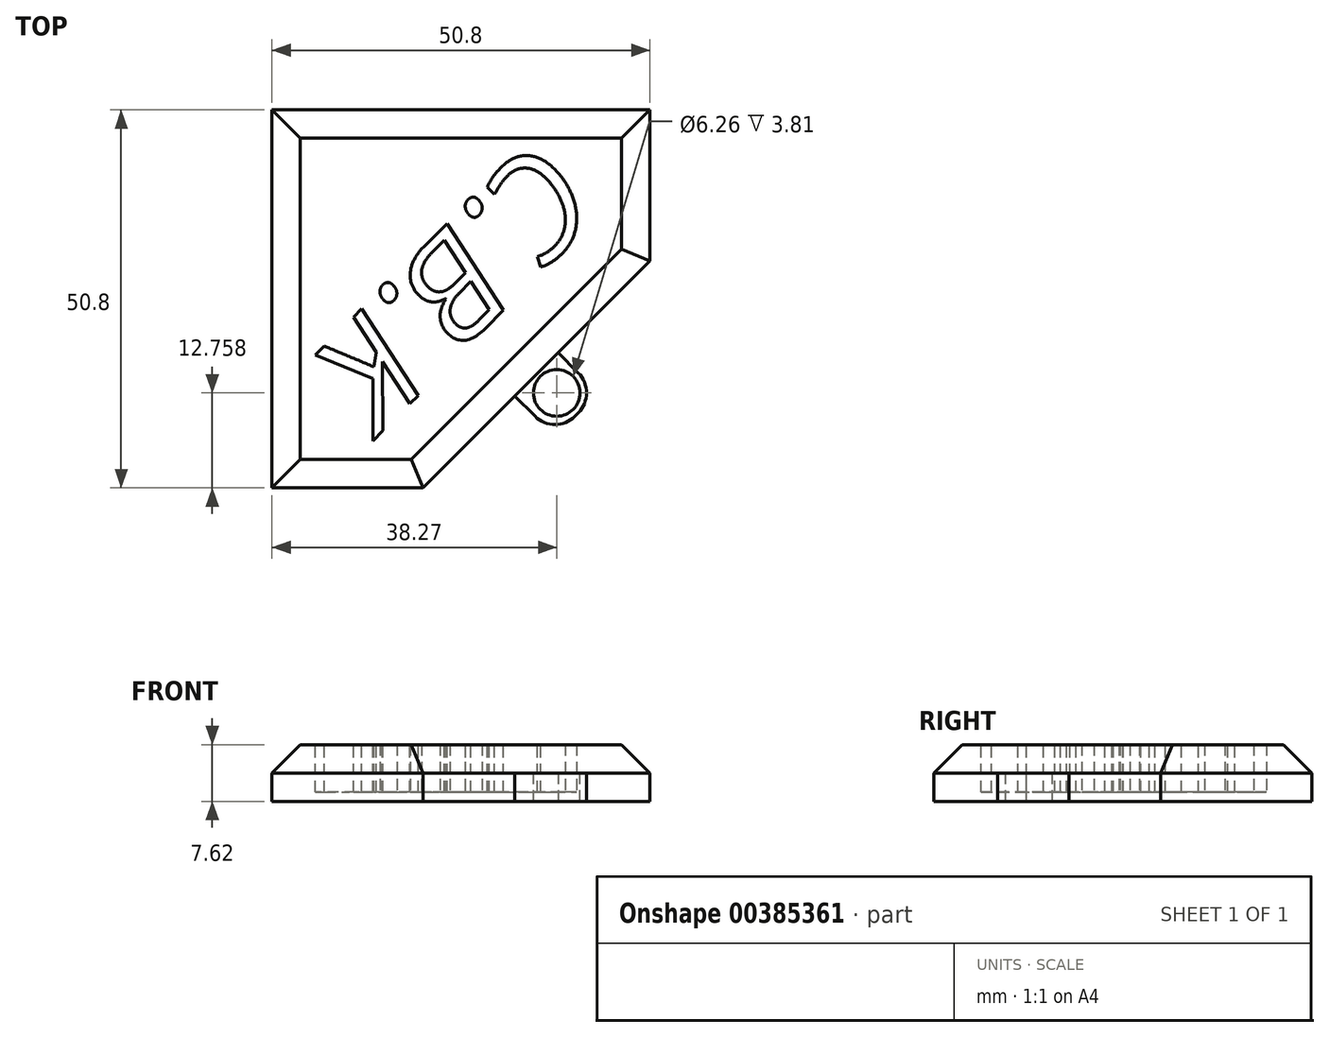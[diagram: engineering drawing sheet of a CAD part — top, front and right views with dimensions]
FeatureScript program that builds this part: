
annotation { "Feature Type Name" : "Feature", "Feature Type Description" : "" }
export const myFeature = defineFeature(function(context is Context, id is Id, definition is map)
    precondition{}
    {
        {
            var Q0;
            Q0=qCreatedBy(makeId("Top.planeOp"),FACE);
            var sketch = newSketch(context, id + "F0", { "sketchPlane" : qUnion([Q0])});
            skLineSegment(sketch, "E0.bottom", {"start": v(0, 0) * mm, "end": v(50.8, 0) * mm});
            skLineSegment(sketch, "E0.top", {"start": v(0, 50.8) * mm, "end": v(50.8, 50.8) * mm});
            skLineSegment(sketch, "E0.left", {"start": v(0, 0) * mm, "end": v(0, 50.8) * mm});
            skLineSegment(sketch, "E0.right", {"start": v(50.8, 0) * mm, "end": v(50.8, 50.8) * mm});
            skSolve(sketch);
        }
        {
            var Q0;
            Q0 = qSketchRegion(id + "F0", true);
            extrude(context, id + "F1", {"entities" : qUnion([Q0]), "oppositeDirection" : true, "depth" : 7.62 * mm});
        }
        {
            var Q0;
            Q0=makeQuery(id+"F1.opExtrude","SWEPT_EDGE",EDGE,{"disambiguationData":[OSD([sQuery(id+"F0.wireOp",EDGE,"E0.bottom"),sQuery(id+"F0.wireOp",EDGE,"E0.right")])]});
            chamfer(context, id + "F2", {"entities" : qUnion([Q0]), "width" : 30.48 * mm, "tangentPropagation" : true});
        }
        {
            var Q0;
            Q0=qCreatedBy(makeId("Top.planeOp"),FACE);
            var sketch = newSketch(context, id + "F3", { "sketchPlane" : qUnion([Q0])});
            skText(sketch, "E1", { "text": "C.B.K", "fontName": "OpenSans-Italic.ttf"});
            const initialGuessF3  = {"E1": [0.03539, 0.0474, -0.70703, -0.70719, 0.01372]};
            skSetInitialGuess(sketch, initialGuessF3);
            skSolve(sketch);
        }
        {
            var Q0;
            Q0 = qSketchRegion(id + "F3", true);
            extrude(context, id + "F4", {"entities" : qUnion([Q0]), "operationType" : NewBodyOperationType.REMOVE, "oppositeDirection" : true, "depth" : 6.35 * mm});
        }
        {
            var Q0;
            Q0=makeQuery(id+"F1.opExtrude","CAP_EDGE",EDGE,{"disambiguationData":[OSD([sQuery(id+"F0.wireOp",EDGE,"E0.right")])],"isStart":true});
            chamfer(context, id + "F5", {"entities" : qUnion([Q0]), "width" : 3.8 * mm, "tangentPropagation" : true});
        }
        {
            var Q0;
            {var subQ0=sQuery(id+"F0.wireOp",EDGE,"E0.right");var subQ1=sQuery(id+"F0.wireOp",EDGE,"E0.bottom");Q0=makeQuery(id+"F2.opChamfer","BLEND_EDGE",EDGE,{"blendedFrom":[makeQuery(id+"F1.opExtrude","SWEPT_EDGE",EDGE,{"disambiguationData":[OSD([subQ1,subQ0])]}),makeQuery(id+"F1.opExtrude","CAP_FACE",FACE,{"disambiguationData":[OSD([subQ1,sQuery(id+"F0.wireOp",EDGE,"E0.top"),sQuery(id+"F0.wireOp",EDGE,"E0.left"),subQ0])],"isStart":true})],"blendedInto":[makeQuery(id+"F1.opExtrude","CAP_FACE",FACE,{"disambiguationData":[OSD([subQ1,sQuery(id+"F0.wireOp",EDGE,"E0.top"),sQuery(id+"F0.wireOp",EDGE,"E0.left"),subQ0])],"isStart":true})]});}
            var Q1;
            Q1=makeQuery(id+"F1.opExtrude","CAP_EDGE",EDGE,{"disambiguationData":[OSD([sQuery(id+"F0.wireOp",EDGE,"E0.bottom")])],"isStart":true});
            var Q2;
            Q2=makeQuery(id+"F1.opExtrude","CAP_EDGE",EDGE,{"disambiguationData":[OSD([sQuery(id+"F0.wireOp",EDGE,"E0.top")])],"isStart":true});
            var Q3;
            Q3=makeQuery(id+"F1.opExtrude","CAP_EDGE",EDGE,{"disambiguationData":[OSD([sQuery(id+"F0.wireOp",EDGE,"E0.left")])],"isStart":true});
            chamfer(context, id + "F6", {"entities" : qUnion([Q0, Q1, Q2, Q3]), "width" : 3.8 * mm, "tangentPropagation" : true});
        }
        {
            var Q0;
            Q0=makeQuery(id+"F2.opChamfer","BLEND_FACE",FACE,{"disambiguationData":[OSD([sQuery(id+"F0.wireOp",EDGE,"E0.bottom"),sQuery(id+"F0.wireOp",EDGE,"E0.right")])]});
            var sketch = newSketch(context, id + "F7", { "sketchPlane" : qUnion([Q0])});
            skLineSegment(sketch, "E2.bottom", {"start": v(31.81, -3.8) * mm, "end": v(40.03, -3.8) * mm});
            skLineSegment(sketch, "E2.top", {"start": v(31.81, -7.62) * mm, "end": v(40.03, -7.62) * mm});
            skLineSegment(sketch, "E2.left", {"start": v(31.81, -3.8) * mm, "end": v(31.81, -7.62) * mm});
            skLineSegment(sketch, "E2.right", {"start": v(40.03, -3.8) * mm, "end": v(40.03, -7.62) * mm});
            skPoint(sketch, "E2.middle", {"position": v(35.92, -5.71) * mm});
            skSolve(sketch);
        }
        {
            var Q0;
            Q0 = qSketchRegion(id + "F7", true);
            extrude(context, id + "F8", {"entities" : qUnion([Q0]), "operationType" : NewBodyOperationType.ADD, "depth" : 7.62 * mm});
        }
        {
            var Q0;
            Q0=makeQuery(id+"F8.opExtrude","SWEPT_FACE",FACE,{"disambiguationData":[OSD([sQuery(id+"F7.wireOp",EDGE,"E2.bottom")])]});
            var sketch = newSketch(context, id + "F9", { "sketchPlane" : qUnion([Q0])});
            skCircle(sketch, "E3", {"center": v(38.27, 12.76) * mm, "radius": 3.13 * mm});
            skSolve(sketch);
        }
        {
            var Q0;
            Q0 = qSketchRegion(id + "F9", true);
            extrude(context, id + "F10", {"entities" : qUnion([Q0]), "operationType" : NewBodyOperationType.REMOVE, "oppositeDirection" : true, "depth" : 254 * mm});
        }
        {
            var Q0;
            Q0=makeQuery(id+"F8.opExtrude","CAP_EDGE",EDGE,{"disambiguationData":[OSD([sQuery(id+"F7.wireOp",EDGE,"E2.right")])],"isStart":false});
            var Q1;
            Q1=makeQuery(id+"F8.opExtrude","CAP_EDGE",EDGE,{"disambiguationData":[OSD([sQuery(id+"F7.wireOp",EDGE,"E2.left")])],"isStart":false});
            fillet(context, id + "F11", {"entities" : qUnion([Q0, Q1]), "radius" : 3.8 * mm, "tangentPropagation" : true, "allowEdgeOverflow" : false});
        }
    });
